# Revit family: M_Ryterna_R40-SM wind
name_source: partatom
category: Doors
revit_build: Autodesk Revit 2018 (Build: 20190510_1515(x64)
units: mm (PartAtom-declared; Revit-internal decimal feet)

## family parameters
Always vertical = Yes
Cut with Voids When Loaded = No
Host = Wall
OmniClass Number = 23.30.10.00
OmniClass Title = Doors
Room Calculation Point = No
Shared = No

## types (1)
- R40-SM H2500W3000
    10th Segment Windows = No
    2nd Segment Windows = No
    3rd Segment Windows = No
    4th Segment Windows = No
    5th Segment Windows = No
    6th Segment Windows = No
    7th Segment Windows = No
    8th Segment Windows = No
    9th Segment Windows = No
    Analytic Construction = <None>
    Beam Material = Steel, Galvanized
    Bottom Gasket Material = Gasket Rubber, Black
    Clearance Zone = Yes
    Desired Window Quantity = 0
    Door Bottom Offset = 30 mm  [stored 0.0984252 ft]
    Door Height = 2480 mm
    Door Inset = 15 mm  [stored 0.0492126 ft]
    Door Type Color Material = M_Garage Door : RAL 9016/RAL 9002
    Guide Track Material = Steel, Galvanized
    Height = 2500 mm  [stored 8.2021 ft]
    Height_True = 2500 mm  [stored 8.2021 ft]
    Horizontal C Track Material = Steel, Galvanized
    Lifting Assembly Cover Material = <By Category>
    Lifting Assembly Hanger Material = Steel, Galvanized
    Lifting Assembly Length = 2781 mm  [stored 9.12402 ft]
    Lifting Type = M_Lifting Assembly_R40-SM : 0
    Lifting Type A = M_Lifting Assembly_R40-SM : 0
    Lifting Type B = M_Lifting Assembly_R40-SM : 1
    Lifting Type C = M_Lifting Assembly_R40-SM : 2
    Manufacturer = UAB “RYTERNA GROUP”
    Optimal Window Quantity = 3
    Power Operator = No
    Power Operator Material = Steel, Galvanized
    Power Operator Position = 3600 mm  [stored 11.811 ft]
    Reel Material = Steel, Galvanized
    Rod Material = Steel, Galvanized
    Roller Holder Material = Steel, Galvanized
    Rough Height = 2510 mm  [stored 8.23491 ft]
    Rough Width = 3040 mm
    Slab Slope = 0.00°
    Slab Slope_True = 0.00°
    Spring Holder Material = Steel, Galvanized
    Spring Material = Steel, Galvanized
    Thickness = 40 mm  [stored 0.131234 ft]
    Top Connection Number = 1
    Top Connection Position = 2853 mm
    Top Connection Spacing = 1489 mm
    Top Gasket Material = Gasket Rubber, Black
    Top Track Length = 3181 mm  [stored 10.4364 ft]
    Triangle Connection Material = Steel, Galvanized
    Type = - : No Windows
    URL = https://www.ryterna.eu
    Vertical L Profile Material = Steel, Galvanized
    Wall Closure = By host
    Warning Message = No
    Width = 3000 mm  [stored 9.84252 ft]
    Width_True = 3000 mm  [stored 9.84252 ft]
    Window Type Number = 0
    Window Type Oval = - : PVC Oval
    Window Type PVC Black 488 = - : PVC Black 488x322
    Window Type PVC White 488 = - : PVC White 488x322
    Window Type Rectangular = - : PVC Rectangular
    Window Type Rectangular Narrow = - : PVC Rectangular Narrow
    Window Type SS154 = - : Stainless Steel 154x154
    Window Type SS234 = - : Stainless Steel 234x234
    Window Type SS314 = - : Stainless Steel 314x314
    Window Type SS804 = - : Stainless Steel 804x154
    Window Type SSd150 = - : Stainless Steel D=150
    Window Type SSd230 = - : Stainless Steel D=230
    Window Type SSd310 = - : Stainless Steel D=310
    Zone A Vertical Distance = 503 mm
    Zone B Horizontal Distance = 186 mm
    Zone B Vertical Distance = 275 mm
    Zone Sloped Thickness = 30 mm  [stored 0.0984252 ft]
    Zone Vertical Thickness = 155 mm  [stored 0.50853 ft]
    h = 110 mm  [stored 0.360892 ft]

note: [stored X ft] marks values corroborated as IEEE doubles in the binary element streams (Revit-internal decimal feet)

## geometry (parser evidence)
native form markers: Sweep x143
no freeform markers — native parametric forms only
